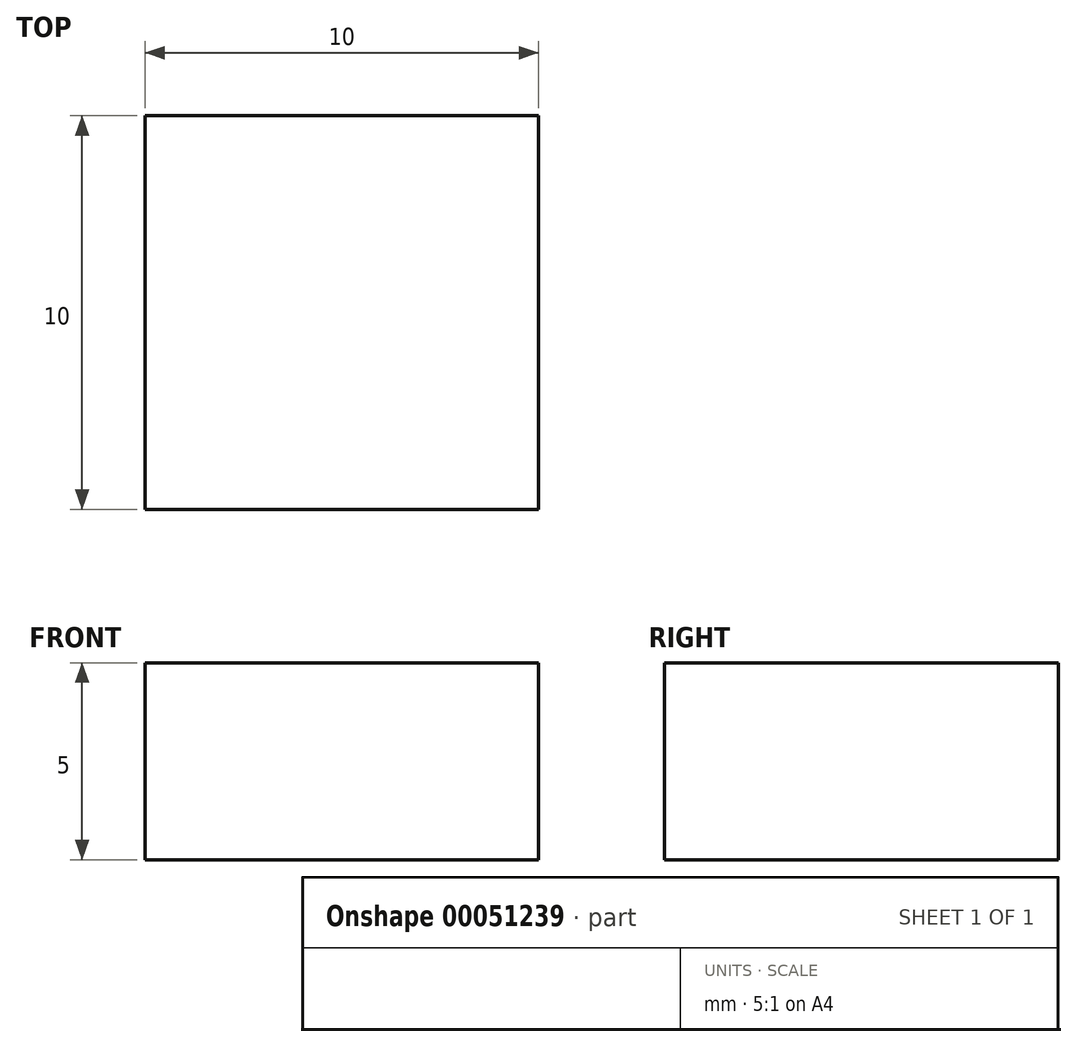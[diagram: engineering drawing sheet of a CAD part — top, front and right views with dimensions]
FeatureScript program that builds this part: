
annotation { "Feature Type Name" : "Feature", "Feature Type Description" : "" }
export const myFeature = defineFeature(function(context is Context, id is Id, definition is map)
    precondition{}
    {
        {
            var Q0;
            Q0=qCreatedBy(makeId("Top.planeOp"),FACE);
            var sketch = newSketch(context, id + "F0", { "sketchPlane" : qUnion([Q0])});
            skLineSegment(sketch, "E0.rect.bottom", {"start": v(5, -5) * mm, "end": v(-5, -5) * mm});
            skLineSegment(sketch, "E0.rect.top", {"start": v(5, 5) * mm, "end": v(-5, 5) * mm});
            skLineSegment(sketch, "E0.rect.left", {"start": v(5, -5) * mm, "end": v(5, 5) * mm});
            skLineSegment(sketch, "E0.rect.right", {"start": v(-5, -5) * mm, "end": v(-5, 5) * mm});
            skPoint(sketch, "E0.rect.middle", {"position": v(0, 0) * mm});
            skSolve(sketch);
        }
        {
            var Q0;
            Q0=makeQuery(id+"F0.imprint","IMPRINT",FACE,{"disambiguationData":[TD([[makeQuery(id+"F0.imprint","IMPRINT",EDGE,{"derivedFrom":sQuery(id+"F0.wireOp",EDGE,"E0.rect.bottom")}),-1.0]])]});
            extrude(context, id + "F1", {"entities" : qUnion([Q0]), "depth" : 5 * mm});
        }
    });
